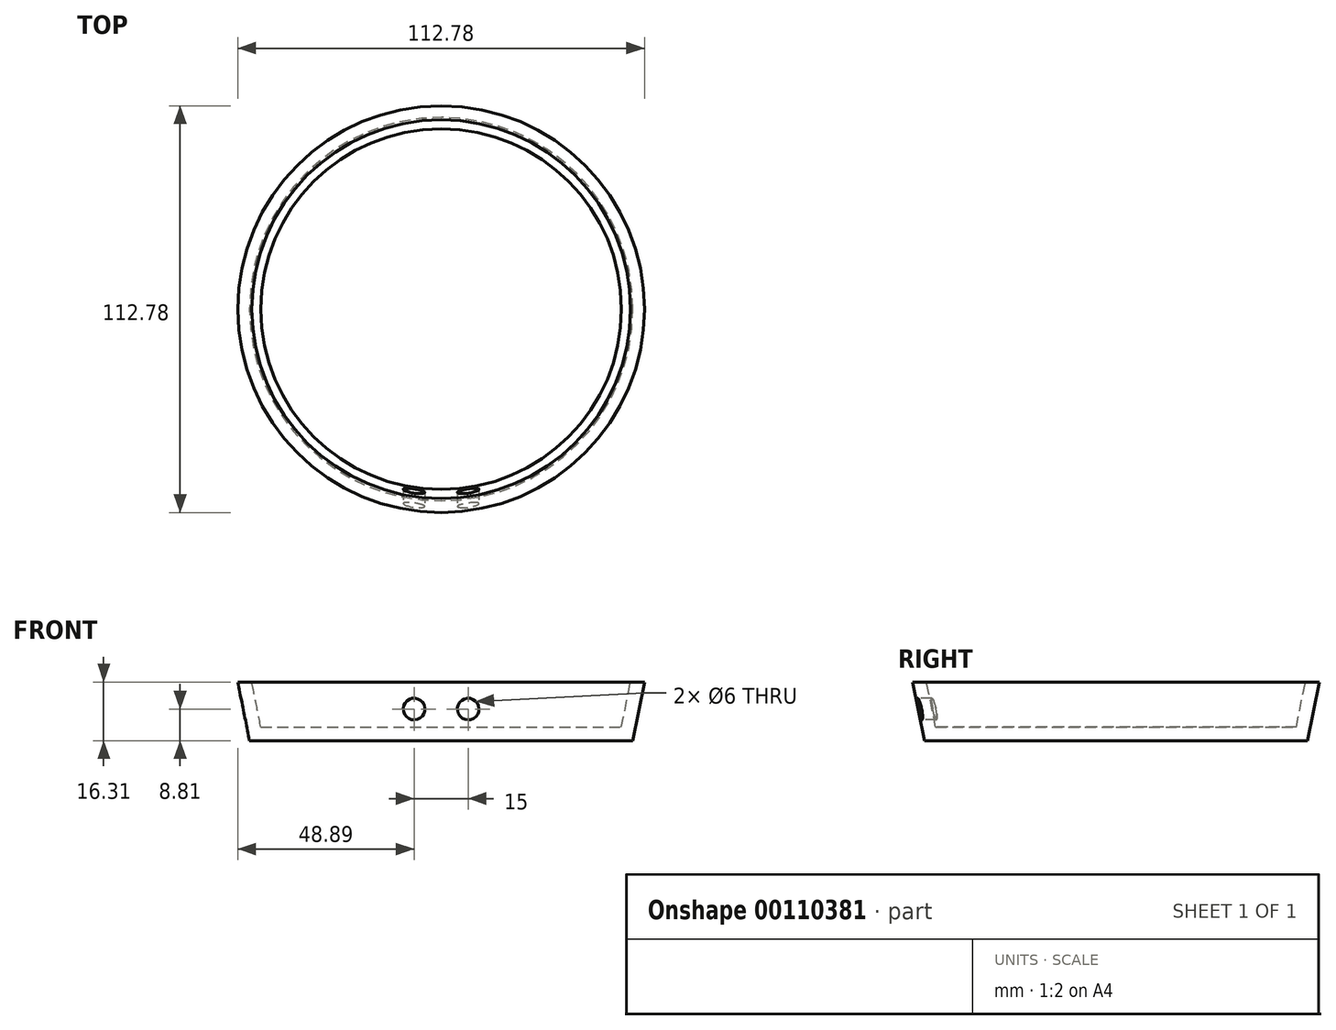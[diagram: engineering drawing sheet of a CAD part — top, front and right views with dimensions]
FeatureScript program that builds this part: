
annotation { "Feature Type Name" : "Feature", "Feature Type Description" : "" }
export const myFeature = defineFeature(function(context is Context, id is Id, definition is map)
    precondition{}
    {
        {
            var Q0;
            Q0=qCreatedBy(makeId("Front.planeOp"),FACE);
            var sketch = newSketch(context, id + "F0", { "sketchPlane" : qUnion([Q0])});
            skLineSegment(sketch, "E0", {"start": v(0, 0) * mm, "end": v(50, 0) * mm});
            skLineSegment(sketch, "E1", {"start": v(0, 0) * mm, "end": v(0, 12.5) * mm, "construction": true});
            skLineSegment(sketch, "E2", {"start": v(0, 12.5) * mm, "end": v(52.5, 12.5) * mm, "construction": true});
            skLineSegment(sketch, "E3", {"start": v(52.5, 12.5) * mm, "end": v(50, 0) * mm});
            skLineSegment(sketch, "E4.0", {"start": v(56.39, 12.5) * mm, "end": v(53.12, -3.81) * mm});
            skLineSegment(sketch, "E5.0", {"start": v(0, -3.81) * mm, "end": v(53.12, -3.81) * mm});
            skLineSegment(sketch, "E6", {"start": v(52.5, 12.5) * mm, "end": v(56.39, 12.5) * mm});
            skLineSegment(sketch, "E7", {"start": v(0, -3.81) * mm, "end": v(0, 0) * mm});
            skSolve(sketch);
        }
        {
            var Q0;
            Q0 = qSketchRegion(id + "F0", true);
            var Q1;
            Q1=sQuery(id+"F0.wireOp",EDGE,"E1");
            revolve(context, id + "F1", {"entities" : qUnion([Q0]), "axis" : qUnion([Q1]), "revolveType" : RevolveType.FULL});
        }
        {
            var Q0;
            Q0=qCreatedBy(makeId("Front.planeOp"),FACE);
            cPlane(context, id + "F2", {"entities" : qUnion([Q0]), "cplaneType" : CPlaneType.OFFSET, "offset" : 56.5 * mm, "width" : 150 * mm, "height" : 150 * mm});
        }
        {
            var Q0;
            Q0=qCreatedBy(id+"F2.planeOp",FACE);
            var sketch = newSketch(context, id + "F3", { "sketchPlane" : qUnion([Q0])});
            skLineSegment(sketch, "E8", {"start": v(0, 0) * mm, "end": v(0, 5) * mm, "construction": true});
            skLineSegment(sketch, "E9", {"start": v(-7.5, 5) * mm, "end": v(7.5, 5) * mm, "construction": true});
            skCircle(sketch, "E10", {"center": v(7.5, 5) * mm, "radius": 3 * mm});
            skCircle(sketch, "E11", {"center": v(-7.5, 5) * mm, "radius": 3 * mm});
            skSolve(sketch);
        }
        {
            var Q0;
            Q0 = qSketchRegion(id + "F3", true);
            extrude(context, id + "F4", {"entities" : qUnion([Q0]), "operationType" : NewBodyOperationType.REMOVE, "oppositeDirection" : true, "depth" : 15 * mm});
        }
    });
